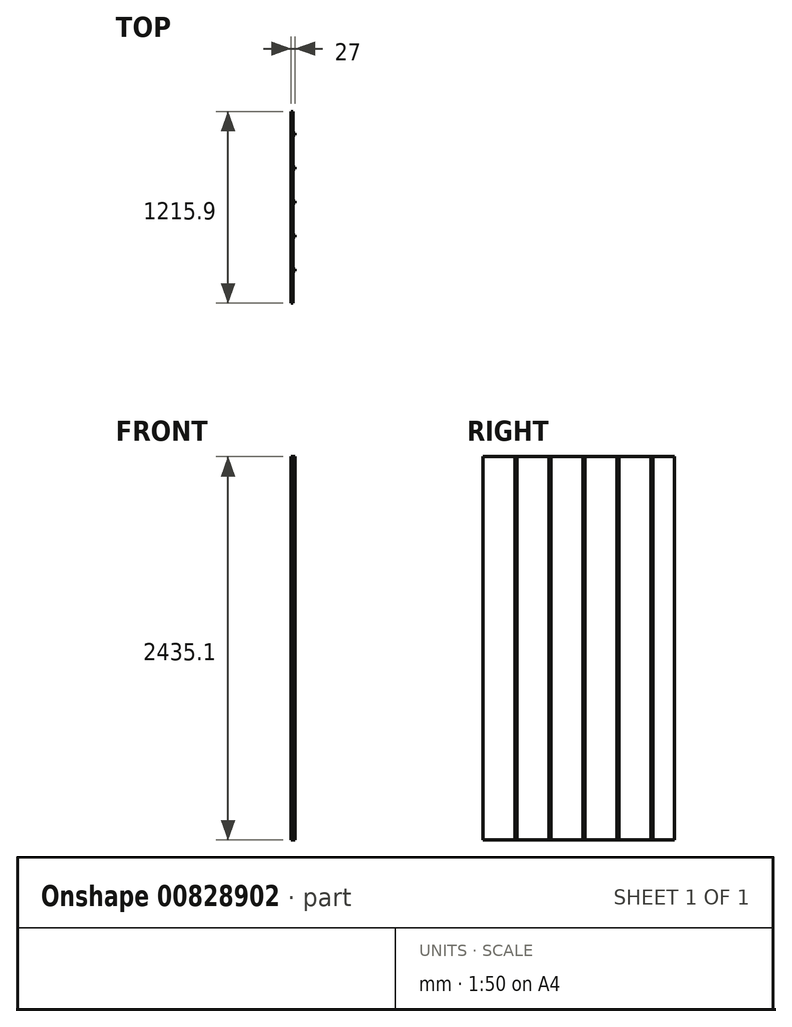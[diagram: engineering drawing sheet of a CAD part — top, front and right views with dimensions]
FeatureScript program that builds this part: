
annotation { "Feature Type Name" : "Feature", "Feature Type Description" : "" }
export const myFeature = defineFeature(function(context is Context, id is Id, definition is map)
    precondition{}
    {
        {
            var Q0;
            Q0=qCreatedBy(makeId("Right.planeOp"),FACE);
            var sketch = newSketch(context, id + "F0", { "sketchPlane" : qUnion([Q0])});
            skLineSegment(sketch, "E0.bottom", {"start": v(0, 0) * mm, "end": v(1215.9, 0) * mm});
            skLineSegment(sketch, "E0.top", {"start": v(0, 2435.1) * mm, "end": v(1215.9, 2435.1) * mm});
            skLineSegment(sketch, "E0.left", {"start": v(0, 0) * mm, "end": v(0, 2435.1) * mm});
            skLineSegment(sketch, "E0.right", {"start": v(1215.9, 0) * mm, "end": v(1215.9, 2435.1) * mm});
            skSolve(sketch);
        }
        {
            var Q0;
            Q0=makeQuery(id+"F0.imprint","IMPRINT",FACE,{"disambiguationData":[TD([[makeQuery(id+"F0.imprint","IMPRINT",EDGE,{"derivedFrom":sQuery(id+"F0.wireOp",EDGE,"E0.bottom")}),1.0]])]});
            var Q1;
            Q1 = qSketchRegion(id + "F2", true);
            extrude(context, id + "F1", {"entities" : qUnion([Q0, Q1]), "depth" : 14.3 * mm, "offsetDistance" : 25.4 * mm});
        }
        {
            var Q0;
            Q0=makeQuery(id+"F1.opExtrude","CAP_FACE",FACE,{"disambiguationData":[OSD([sQuery(id+"F0.wireOp",EDGE,"E0.bottom"),sQuery(id+"F0.wireOp",EDGE,"E0.top"),sQuery(id+"F0.wireOp",EDGE,"E0.left"),sQuery(id+"F0.wireOp",EDGE,"E0.right")])],"isStart":false});
            var sketch = newSketch(context, id + "F2", { "sketchPlane" : qUnion([Q0])});
            skLineSegment(sketch, "E1.bottom", {"start": v(203.2, 2435.1) * mm, "end": v(215.9, 2435.1) * mm});
            skLineSegment(sketch, "E1.top", {"start": v(203.2, 0) * mm, "end": v(215.9, 0) * mm});
            skLineSegment(sketch, "E1.left", {"start": v(203.2, 2435.1) * mm, "end": v(203.2, 0) * mm});
            skLineSegment(sketch, "E1.right", {"start": v(215.9, 2435.1) * mm, "end": v(215.9, 0) * mm});
            skLineSegment(sketch, "E2", {"start": v(215.9, 2435.1) * mm, "end": v(419.1, 2435.1) * mm, "construction": true});
            skLineSegment(sketch, "E3.bottom", {"start": v(419.1, 2435.1) * mm, "end": v(431.8, 2435.1) * mm});
            skLineSegment(sketch, "E3.top", {"start": v(419.1, 0) * mm, "end": v(431.8, 0) * mm});
            skLineSegment(sketch, "E3.left", {"start": v(419.1, 2435.1) * mm, "end": v(419.1, 0) * mm});
            skLineSegment(sketch, "E3.right", {"start": v(431.8, 2435.1) * mm, "end": v(431.8, 0) * mm});
            skLineSegment(sketch, "E4", {"start": v(431.8, 2435.1) * mm, "end": v(635, 2435.1) * mm, "construction": true});
            skLineSegment(sketch, "E5.bottom", {"start": v(635, 2435.1) * mm, "end": v(647.7, 2435.1) * mm});
            skLineSegment(sketch, "E5.top", {"start": v(635, 0) * mm, "end": v(647.7, 0) * mm});
            skLineSegment(sketch, "E5.left", {"start": v(635, 2435.1) * mm, "end": v(635, 0) * mm});
            skLineSegment(sketch, "E5.right", {"start": v(647.7, 2435.1) * mm, "end": v(647.7, 0) * mm});
            skLineSegment(sketch, "E6", {"start": v(647.7, 2435.1) * mm, "end": v(850.9, 2435.1) * mm, "construction": true});
            skLineSegment(sketch, "E7.bottom", {"start": v(850.9, 2435.1) * mm, "end": v(863.6, 2435.1) * mm});
            skLineSegment(sketch, "E7.top", {"start": v(850.9, 0) * mm, "end": v(863.6, 0) * mm});
            skLineSegment(sketch, "E7.left", {"start": v(850.9, 2435.1) * mm, "end": v(850.9, 0) * mm});
            skLineSegment(sketch, "E7.right", {"start": v(863.6, 2435.1) * mm, "end": v(863.6, 0) * mm});
            skLineSegment(sketch, "E8", {"start": v(863.6, 2435.1) * mm, "end": v(1066.8, 2435.1) * mm, "construction": true});
            skLineSegment(sketch, "E9.bottom", {"start": v(1066.8, 2435.1) * mm, "end": v(1079.5, 2435.1) * mm});
            skLineSegment(sketch, "E9.top", {"start": v(1066.8, 0) * mm, "end": v(1079.5, 0) * mm});
            skLineSegment(sketch, "E9.left", {"start": v(1066.8, 2435.1) * mm, "end": v(1066.8, 0) * mm});
            skLineSegment(sketch, "E9.right", {"start": v(1079.5, 2435.1) * mm, "end": v(1079.5, 0) * mm});
            skSolve(sketch);
        }
        {
            var Q0;
            Q0=makeQuery(id+"F2.imprint","IMPRINT",FACE,{"disambiguationData":[TD([[makeQuery(id+"F2.imprint","IMPRINT",EDGE,{"derivedFrom":sQuery(id+"F2.wireOp",EDGE,"E3.bottom")}),-1.0]])]});
            var Q1;
            Q1=makeQuery(id+"F2.imprint","IMPRINT",FACE,{"disambiguationData":[TD([[makeQuery(id+"F2.imprint","IMPRINT",EDGE,{"derivedFrom":sQuery(id+"F2.wireOp",EDGE,"E5.bottom")}),-1.0]])]});
            var Q2;
            Q2=makeQuery(id+"F2.imprint","IMPRINT",FACE,{"disambiguationData":[TD([[makeQuery(id+"F2.imprint","IMPRINT",EDGE,{"derivedFrom":sQuery(id+"F2.wireOp",EDGE,"E7.bottom")}),-1.0]])]});
            var Q3;
            Q3=makeQuery(id+"F2.imprint","IMPRINT",FACE,{"disambiguationData":[TD([[makeQuery(id+"F2.imprint","IMPRINT",EDGE,{"derivedFrom":sQuery(id+"F2.wireOp",EDGE,"E9.bottom")}),-1.0]])]});
            var Q4;
            Q4=makeQuery(id+"F2.imprint","IMPRINT",FACE,{"disambiguationData":[TD([[makeQuery(id+"F2.imprint","IMPRINT",EDGE,{"derivedFrom":sQuery(id+"F2.wireOp",EDGE,"E1.bottom")}),-1.0]])]});
            extrude(context, id + "F3", {"entities" : qUnion([Q0, Q1, Q2, Q3, Q4]), "operationType" : NewBodyOperationType.ADD, "depth" : 12.7 * mm, "offsetDistance" : 25.4 * mm});
        }
    });
